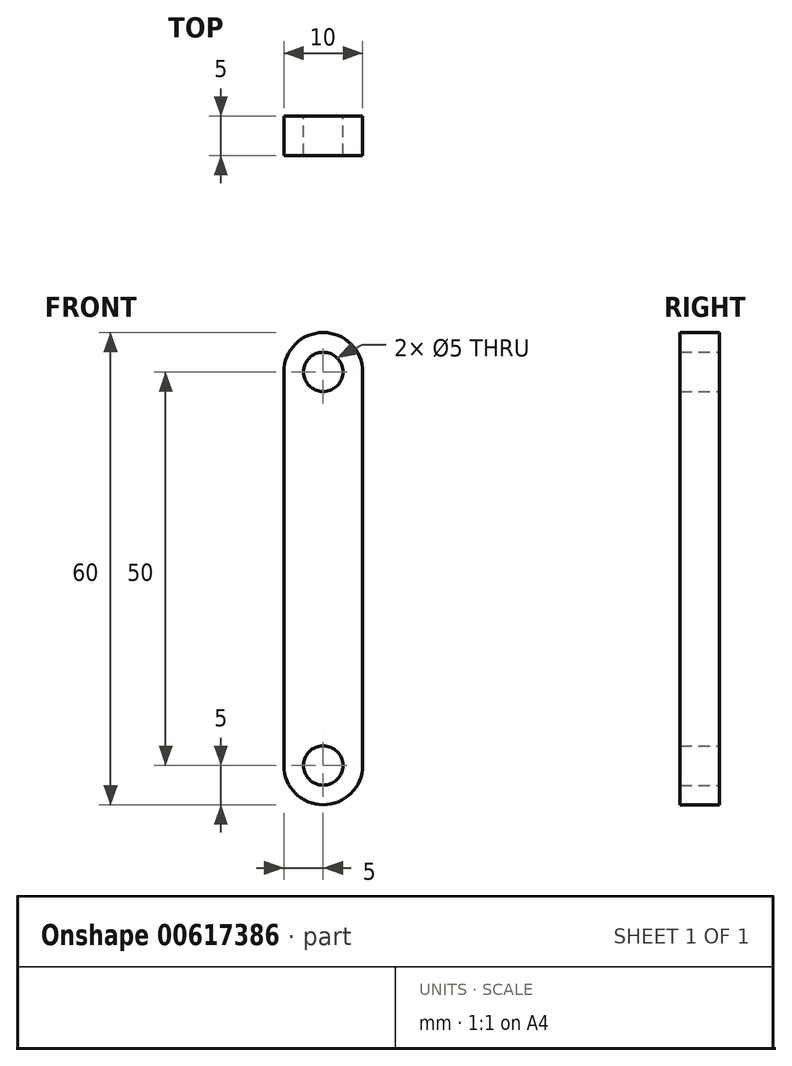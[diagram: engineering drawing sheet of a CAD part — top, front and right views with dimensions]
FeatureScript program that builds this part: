
annotation { "Feature Type Name" : "Feature", "Feature Type Description" : "" }
export const myFeature = defineFeature(function(context is Context, id is Id, definition is map)
    precondition{}
    {
        {
            var Q0;
            Q0=qCreatedBy(makeId("Front.planeOp"),FACE);
            var sketch = newSketch(context, id + "F0", { "sketchPlane" : qUnion([Q0])});
            skArc(sketch, "E0", {"start": v(-5, 0) * mm, "mid": v(0, -5) * mm, "end": v(5, 0) * mm});
            skArc(sketch, "E1", {"start": v(5, 50) * mm, "mid": v(0, 55) * mm, "end": v(-5, 50) * mm});
            skLineSegment(sketch, "E2", {"start": v(-5, 50) * mm, "end": v(-5, 0) * mm});
            skLineSegment(sketch, "E3", {"start": v(5, 50) * mm, "end": v(5, 0) * mm});
            skCircle(sketch, "E4", {"center": v(0, 50) * mm, "radius": 2.5 * mm});
            skCircle(sketch, "E5", {"center": v(0, 0) * mm, "radius": 2.5 * mm});
            skSolve(sketch);
        }
        {
            var Q0;
            Q0=makeQuery(id+"F0.imprint","IMPRINT",FACE,{"disambiguationData":[TD([[makeQuery(id+"F0.imprint","IMPRINT",EDGE,{"derivedFrom":sQuery(id+"F0.wireOp",EDGE,"E0")}),1.0]])]});
            extrude(context, id + "F1", {"entities" : qUnion([Q0]), "depth" : 5 * mm, "offsetDistance" : 25 * mm});
        }
    });
